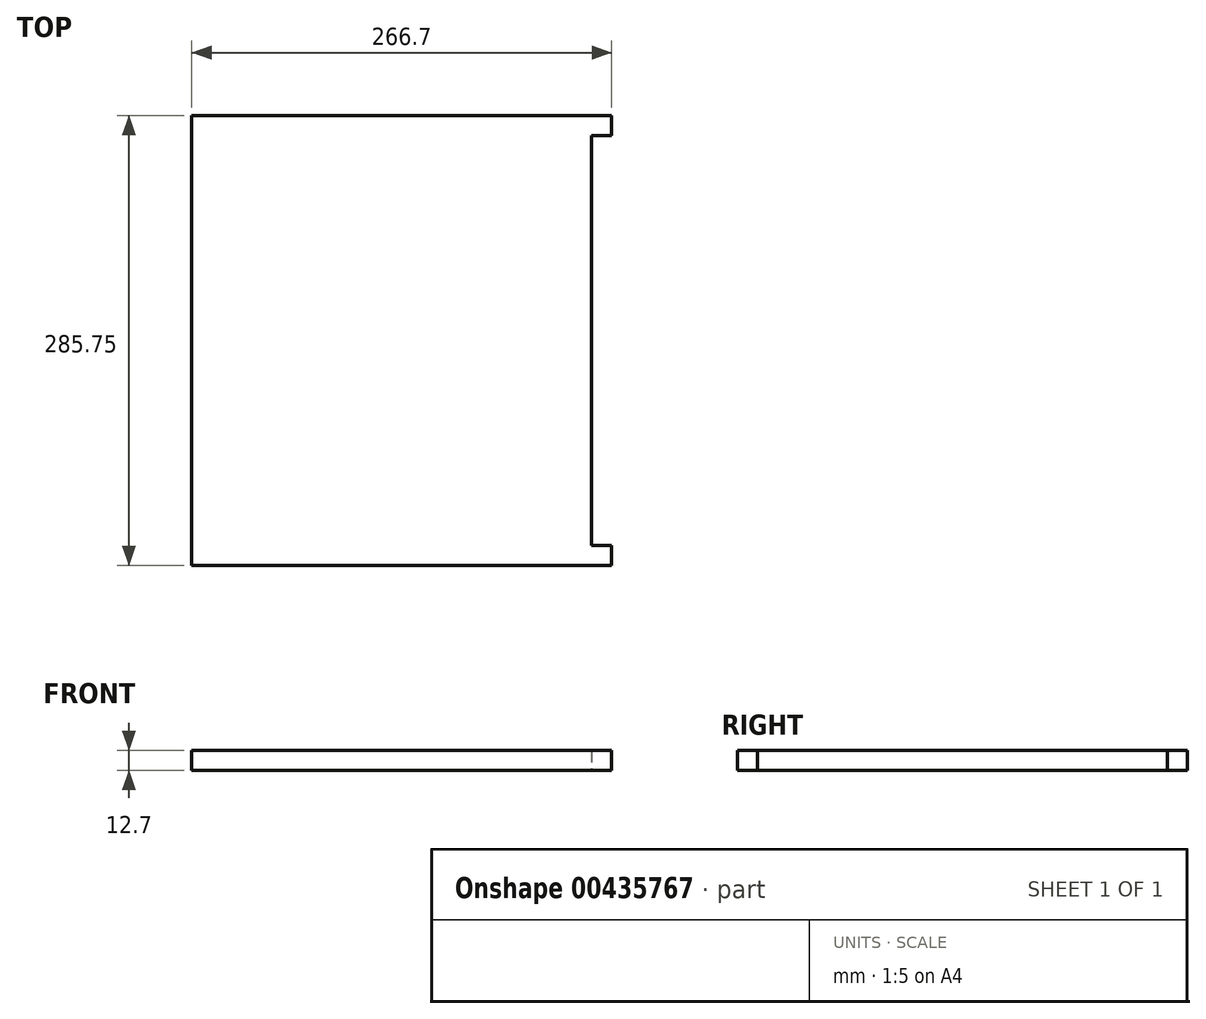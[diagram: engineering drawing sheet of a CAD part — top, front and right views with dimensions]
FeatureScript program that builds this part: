
annotation { "Feature Type Name" : "Feature", "Feature Type Description" : "" }
export const myFeature = defineFeature(function(context is Context, id is Id, definition is map)
    precondition{}
    {
        {
            var Q0;
            Q0=qCreatedBy(makeId("Top.planeOp"),FACE);
            var sketch = newSketch(context, id + "F0", { "sketchPlane" : qUnion([Q0])});
            skLineSegment(sketch, "E0.left", {"start": v(-127, -73.02) * mm, "end": v(-127, -358.78) * mm});
            skLineSegment(sketch, "E1.trimOffspring", {"start": v(127, -280.84) * mm, "end": v(127, -346.07) * mm});
            skLineSegment(sketch, "E2", {"start": v(139.7, -85.72) * mm, "end": v(139.7, -73.02) * mm});
            skLineSegment(sketch, "E3", {"start": v(139.7, -85.72) * mm, "end": v(127, -85.72) * mm});
            skLineSegment(sketch, "E4", {"start": v(127, -358.78) * mm, "end": v(139.7, -358.77) * mm});
            skLineSegment(sketch, "E5", {"start": v(139.7, -358.78) * mm, "end": v(139.7, -346.08) * mm});
            skLineSegment(sketch, "E6", {"start": v(139.7, -346.07) * mm, "end": v(127, -346.07) * mm});
            skLineSegment(sketch, "E7.trimOffspring", {"start": v(127, -85.72) * mm, "end": v(127, -280.84) * mm});
            skPoint(sketch, "E8", {"position": v(0, 0) * mm});
            skLineSegment(sketch, "E9", {"start": v(127, -358.78) * mm, "end": v(-127, -358.78) * mm});
            skLineSegment(sketch, "E10", {"start": v(139.7, -73.02) * mm, "end": v(127, -73.02) * mm});
            skLineSegment(sketch, "E11", {"start": v(127, -73.02) * mm, "end": v(-127, -73.02) * mm});
            skSolve(sketch);
        }
        {
            var Q0;
            Q0=makeQuery(id+"F0.imprint","IMPRINT",FACE,{"disambiguationData":[TD([[makeQuery(id+"F0.imprint","IMPRINT",EDGE,{"derivedFrom":sQuery(id+"F0.wireOp",EDGE,"E0.left")}),1.0]])]});
            extrude(context, id + "F1", {"entities" : qUnion([Q0]), "depth" : 12.7 * mm});
        }
    });
